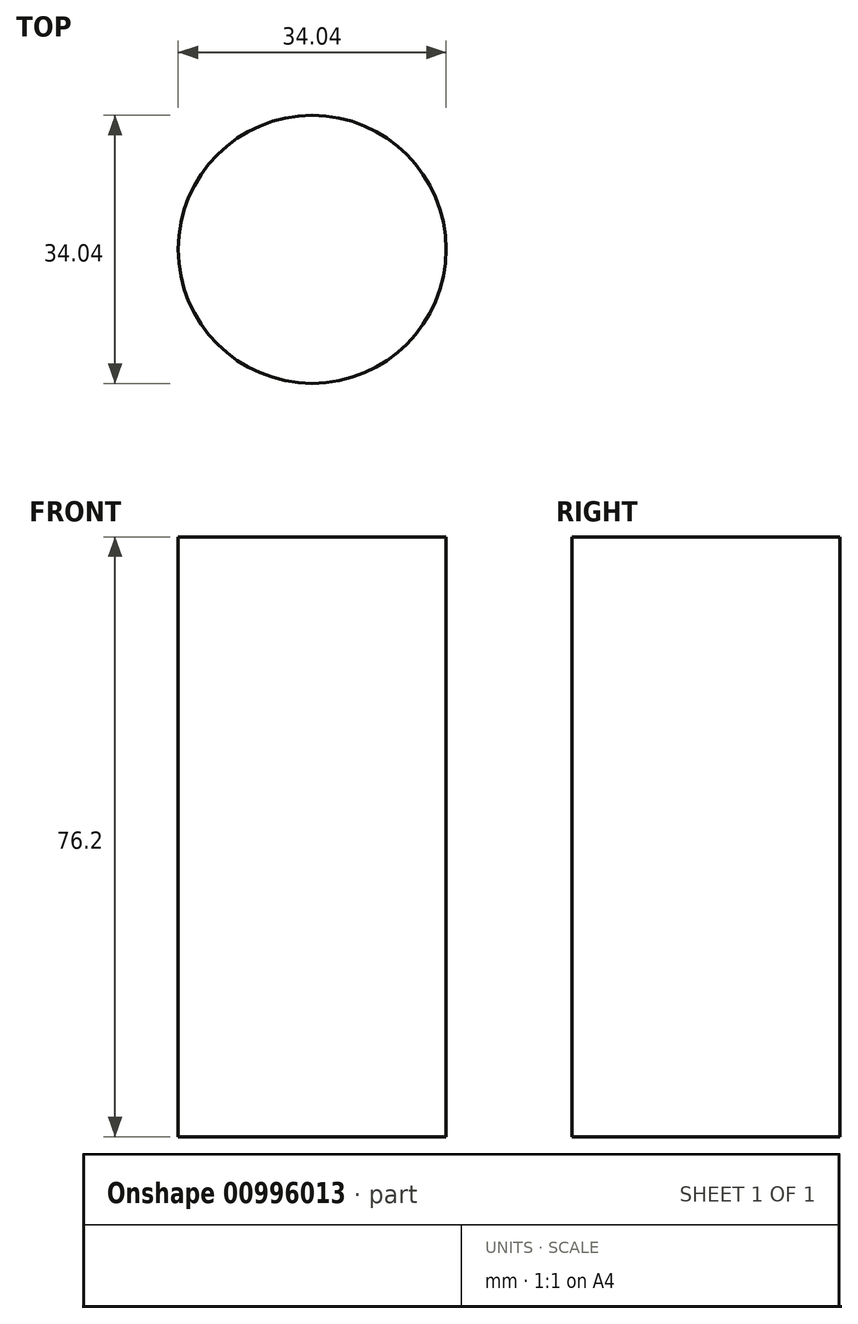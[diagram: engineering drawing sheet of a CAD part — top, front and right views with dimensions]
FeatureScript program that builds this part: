
annotation { "Feature Type Name" : "Feature", "Feature Type Description" : "" }
export const myFeature = defineFeature(function(context is Context, id is Id, definition is map)
    precondition{}
    {
        {
            var Q0;
            Q0=qCreatedBy(makeId("Top.planeOp"),FACE);
            var sketch = newSketch(context, id + "F0", { "sketchPlane" : qUnion([Q0])});
            skCircle(sketch, "E0", {"center": v(0, 0) * mm, "radius": 17.02 * mm});
            skSolve(sketch);
        }
        {
            var Q0;
            Q0=makeQuery(id+"F0.imprint","IMPRINT",FACE,{"disambiguationData":[TD([[makeQuery(id+"F0.imprint","IMPRINT",EDGE,{"derivedFrom":sQuery(id+"F0.wireOp",EDGE,"E0")}),1.0]])]});
            extrude(context, id + "F1", {"entities" : qUnion([Q0]), "depth" : 76.2 * mm, "offsetDistance" : 25 * mm});
        }
    });
